# Revit family: Firestop-cast_in_place-STI-Plastic_Pipes_new
name_source: partatom
category: Specialty Equipment
units: mm (PartAtom-declared; Revit-internal decimal feet)

## family parameters
Always vertical = Yes
Classification Number = 23.20.50.14.11
Cut with Voids When Loaded = No
Enable Cutting in Views = No
Host = Floor
Maintain Annotation Orientation = No
Part Type = Normal
Room Calculation Point = No
Round Connector Dimension = Use Diameter
Shared = No

## types (3) — shared parameters
Assembly Code = D4030900
Color = Red
Default Elevation = 0' - 0"
Dimensions (Overall, devices) = 5-1/8" x 5-1/8" x 8"
Fire Rating = Up to 3 Hr
Green Building/LEED® Information = http://files.systems.stifirestop.com
Guide Specification = http://www.stifirestop.com
Locate Distributor = http://www.stifirestop.com
MSDS = http://files.systems.stifirestop.com
Manufacturer = Specified Technologies Inc.
Manufacturer Fax No. = 908.526.9623
Material = Polypropylene
Model = Cast in place
Plastici-STI-Plastici-Pipe-Cast-in = Cast-In Plastic Pipe bottom
Plastici-STI-Plastici-top cast-in = Cast-In Plastic Pipe top
Product Documentation Link = http://files.systems.stifirestop.com
Product Page URL = http://www.stifirestop.com
Tested Systems = http://sti.fmpdata.net
URL = http://www.stifirestop.com

## per-type parameters (varying)
| type | Description | Flange Sq | Inside ID | Upper OD | base OD | base hight |
| pipe 2 | One 2" Trade Size Cast-in Firestop Device for Combustible & Noncombustible Penetrants | 0' - 4 5/32" | 0' - 2 29/32" | 0' - 3 1/8" | 0' - 3 21/32" | 0' - 2 1/4" |
| pipe 3 | One 3" Trade Size Cast-in Firestop Device for Combustible & Noncombustible Penetrants | 0' - 5 3/4" | 0' - 3 29/32" | 0' - 4 1/16" | 0' - 5 11/32" | 0' - 2 3/32" |
| pipe 4 | One 4" Trade Size Cast-in Firestop Device for Combustible & Noncombustible Penetrants | 0' - 6 3/4" | 0' - 4 15/16" | 0' - 5 1/8" | 0' - 6 3/8" | 0' - 2 9/32" |

## geometry (parser evidence)
native form markers: Blend x18, Sweep x2
no freeform markers — native parametric forms only
